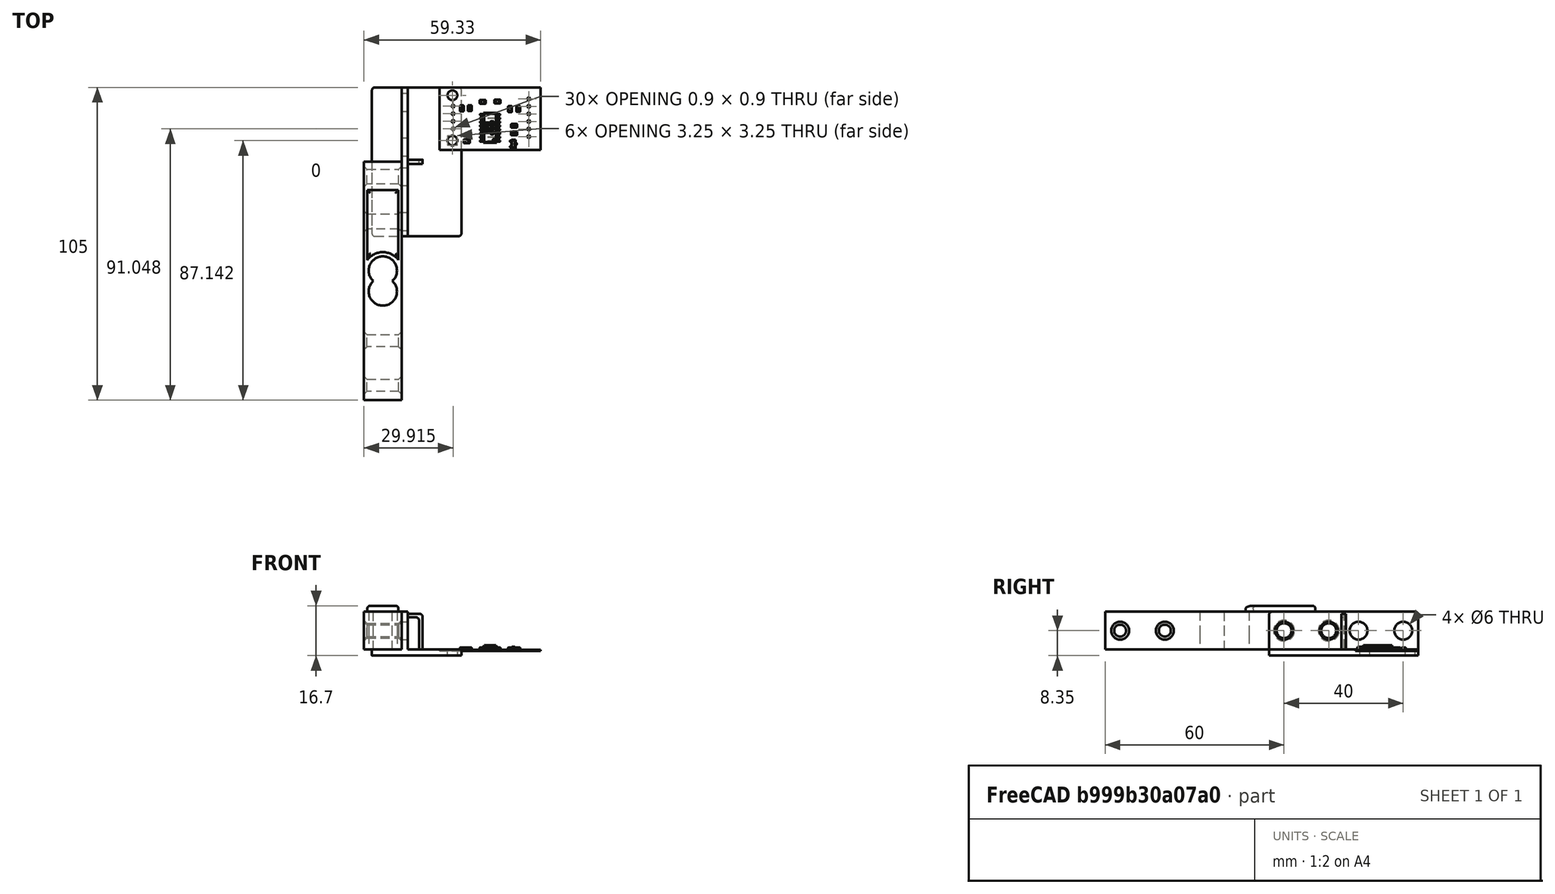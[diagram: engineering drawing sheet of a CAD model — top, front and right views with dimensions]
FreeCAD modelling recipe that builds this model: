
FCSTD DOCUMENT  (FreeCAD 0.19R24267 +148 (Git))
Label: assembly_V3
License: All rights reserved
LicenseURL: http://en.wikipedia.org/wiki/All_rights_reserved
objects: App::FeaturePython×8, Part::FeaturePython×3, PartDesign::FeatureBase×1, PartDesign::Body×1
note: 5 computed .brp shape members not serialized (recipe doc carries the construction recipe); baked Part::Feature solids carry a one-line shape summary decoded from their .brp

FEATURE [Part::FeaturePython] b__xd1_x82_xd0_xb5_xd0_xbd_xd0_xb7_xd0_xbe_xd0_xb4_xd0_xb0_xd1_x82_xd1_x87_xd0_xb8_xd0_xba__xd0_xbc_xd0_xbe_xd0_xb4_xd0_xb5_xd0_xbb_xd1_x8c_001_  label="тензодатчик модель_001"  # a2plus imported part (geometry in sourceFile) (typed FeaturePython)
  Placement = pos=(10,105,14.7) rot=(0.707107,-0.707107,0;3.14159rad)
  a2p_Version = V0.1
  fixedPosition = false
  objectType = a2pPart
  sourceFile = .\тензодатчик модель.FCStd
  subassemblyImport = false
  timeLastImport = 1.65275e+09
  updateColors = true
FEATURE [Part::FeaturePython] b_HX711_001_  label="HX711_001"  # a2plus imported part (geometry in sourceFile) (typed FeaturePython)
  Placement = pos=(56.625,50,1.5) rot=(0,0,1;3.14159rad)
  a2p_Version = V0.1
  fixedPosition = false
  objectType = a2pPart
  sourceFile = .\HX711.FCStd
  subassemblyImport = false
  timeLastImport = 1.65281e+09
  updateColors = true
FEATURE [Part::FeaturePython] b__xd0_xb4_xd0_xb5_xd1_x80_xd0_xb6_xd0_xb0_xd1_x82_xd0_xb5_xd0_xbb_xd1_x8c_V3_001_  label="держатель_V3_001"  # a2plus imported part (geometry in sourceFile) (typed FeaturePython)
  a2p_Version = V0.1
  fixedPosition = true
  objectType = a2pPart
  sourceFile = .\держатель_V3.FCStd
  subassemblyImport = false
  timeLastImport = 1.65281e+09
  updateColors = true
FEATURE [PartDesign::FeatureBase] Clone
  BaseFeature = -> b__xd1_x82_xd0_xb5_xd0_xbd_xd0_xb7_xd0_xbe_xd0_xb4_xd0_xb0_xd1_x82_xd1_x87_xd0_xb8_xd0_xba__xd0_xbc_xd0_xbe_xd0_xb4_xd0_xb5_xd0_xbb_xd1_x8c_001_
  Placement = pos=(2.7,94,14.7) rot=(0.707107,-0.707107,0;3.14159rad)
FEATURE [PartDesign::Body] Body  label="тензодатчик модель_002"
  Group = -> [Clone]
  Origin = -> Origin
  Placement = pos=(4e-14,39,0) rot=(0,0,1;3.14159rad)
  Tip = -> Clone
FEATURE [App::FeaturePython] planeCoincident_001  label="planeCoincident_001__держатель_V3_001"  # a2plus constraint (typed FeaturePython)
  Object1 = Clone
  Object2 = b__xd0_xb4_xd0_xb5_xd1_x80_xd0_xb6_xd0_xb0_xd1_x82_xd0_xb5_xd0_xbb_xd1_x8c_V3_001_
  ParentTreeObject = -> Clone
  SubElement1 = Face21
  SubElement2 = Face17
  Suppressed = false
  Type = plane
  directionConstraint = 1
  offset = 0
FEATURE [App::FeaturePython] planeCoincident_001_mirror  label="planeCoincident_001__Clone"  # a2plus constraint (typed FeaturePython)
  Object1 = Clone
  Object2 = b__xd0_xb4_xd0_xb5_xd1_x80_xd0_xb6_xd0_xb0_xd1_x82_xd0_xb5_xd0_xbb_xd1_x8c_V3_001_
  ParentTreeObject = -> b__xd0_xb4_xd0_xb5_xd1_x80_xd0_xb6_xd0_xb0_xd1_x82_xd0_xb5_xd0_xbb_xd1_x8c_V3_001_
  SubElement1 = Face21
  SubElement2 = Face17
  Suppressed = false
  Type = plane
  directionConstraint = 1
  offset = 0
FEATURE [App::FeaturePython] planeCoincident_002  label="planeCoincident_002__держатель_V3_001"  # a2plus constraint (typed FeaturePython)
  Object1 = Clone
  Object2 = b__xd0_xb4_xd0_xb5_xd1_x80_xd0_xb6_xd0_xb0_xd1_x82_xd0_xb5_xd0_xbb_xd1_x8c_V3_001_
  ParentTreeObject = -> Clone
  SubElement1 = Face13
  SubElement2 = Face37
  Suppressed = false
  Type = plane
  directionConstraint = 1
  offset = 0
FEATURE [App::FeaturePython] planeCoincident_002_mirror  label="planeCoincident_002__Clone"  # a2plus constraint (typed FeaturePython)
  Object1 = Clone
  Object2 = b__xd0_xb4_xd0_xb5_xd1_x80_xd0_xb6_xd0_xb0_xd1_x82_xd0_xb5_xd0_xbb_xd1_x8c_V3_001_
  ParentTreeObject = -> b__xd0_xb4_xd0_xb5_xd1_x80_xd0_xb6_xd0_xb0_xd1_x82_xd0_xb5_xd0_xbb_xd1_x8c_V3_001_
  SubElement1 = Face13
  SubElement2 = Face37
  Suppressed = false
  Type = plane
  directionConstraint = 1
  offset = 0
FEATURE [App::FeaturePython] planeCoincident_003  label="planeCoincident_003__Clone"  # a2plus constraint (typed FeaturePython)
  Object1 = b__xd0_xb4_xd0_xb5_xd1_x80_xd0_xb6_xd0_xb0_xd1_x82_xd0_xb5_xd0_xbb_xd1_x8c_V3_001_
  Object2 = Clone
  ParentTreeObject = -> b__xd0_xb4_xd0_xb5_xd1_x80_xd0_xb6_xd0_xb0_xd1_x82_xd0_xb5_xd0_xbb_xd1_x8c_V3_001_
  SubElement1 = Face37
  SubElement2 = Face13
  Suppressed = false
  Type = plane
  directionConstraint = 1
  offset = 0
FEATURE [App::FeaturePython] planeCoincident_003_mirror  label="planeCoincident_003__держатель_V3_001"  # a2plus constraint (typed FeaturePython)
  Object1 = b__xd0_xb4_xd0_xb5_xd1_x80_xd0_xb6_xd0_xb0_xd1_x82_xd0_xb5_xd0_xbb_xd1_x8c_V3_001_
  Object2 = Clone
  ParentTreeObject = -> Clone
  SubElement1 = Face37
  SubElement2 = Face13
  Suppressed = false
  Type = plane
  directionConstraint = 1
  offset = 0
FEATURE [App::FeaturePython] planeCoincident_004  label="planeCoincident_004__Clone"  # a2plus constraint (typed FeaturePython)
  Object1 = b__xd0_xb4_xd0_xb5_xd1_x80_xd0_xb6_xd0_xb0_xd1_x82_xd0_xb5_xd0_xbb_xd1_x8c_V3_001_
  Object2 = Clone
  ParentTreeObject = -> b__xd0_xb4_xd0_xb5_xd1_x80_xd0_xb6_xd0_xb0_xd1_x82_xd0_xb5_xd0_xbb_xd1_x8c_V3_001_
  SubElement1 = Face17
  SubElement2 = Face21
  Suppressed = false
  Type = plane
  directionConstraint = 1
  offset = 0
FEATURE [App::FeaturePython] planeCoincident_004_mirror  label="planeCoincident_004__держатель_V3_001"  # a2plus constraint (typed FeaturePython)
  Object1 = b__xd0_xb4_xd0_xb5_xd1_x80_xd0_xb6_xd0_xb0_xd1_x82_xd0_xb5_xd0_xbb_xd1_x8c_V3_001_
  Object2 = Clone
  ParentTreeObject = -> Clone
  SubElement1 = Face17
  SubElement2 = Face21
  Suppressed = false
  Type = plane
  directionConstraint = 1
  offset = 0
